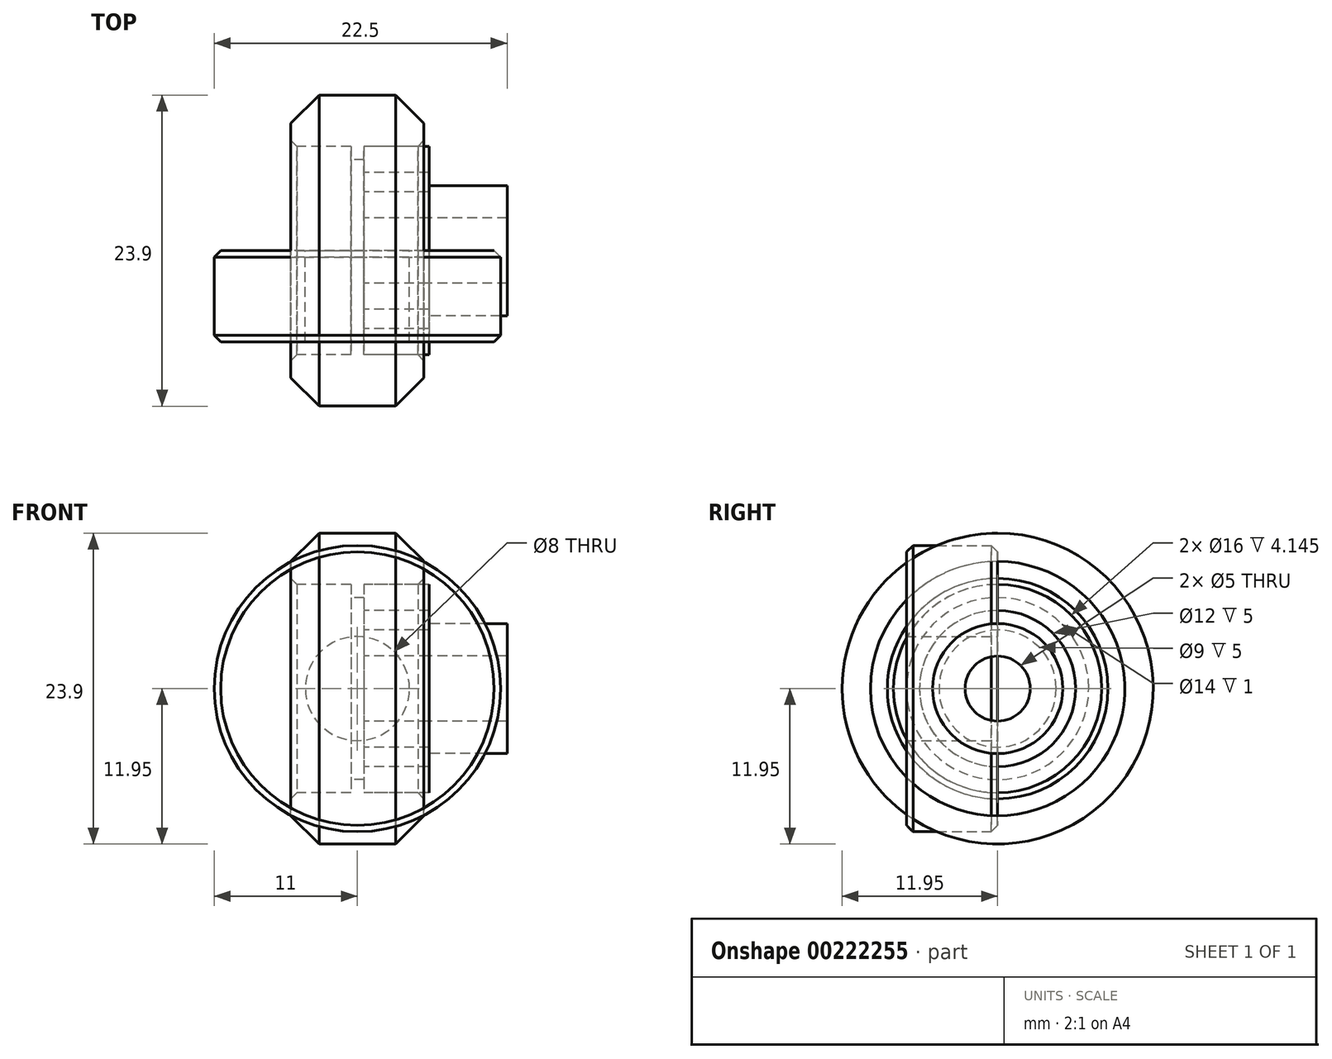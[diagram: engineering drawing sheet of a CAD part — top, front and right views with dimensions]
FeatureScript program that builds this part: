
annotation { "Feature Type Name" : "Feature", "Feature Type Description" : "" }
export const myFeature = defineFeature(function(context is Context, id is Id, definition is map)
    precondition{}
    {
        {
            var Q0;
            Q0=qCreatedBy(makeId("Front.planeOp"),FACE);
            var sketch = newSketch(context, id + "F0", { "sketchPlane" : qUnion([Q0])});
            skLineSegment(sketch, "E0", {"start": v(-1.34, 0) * mm, "end": v(1.5, 0) * mm});
            skLineSegment(sketch, "E1", {"start": v(-2.95, 11.95) * mm, "end": v(2.94, 11.95) * mm});
            skLineSegment(sketch, "E2", {"start": v(2.94, 11.94) * mm, "end": v(5.11, 9.77) * mm});
            skLineSegment(sketch, "E3", {"start": v(5.12, 9.77) * mm, "end": v(5.12, 8.47) * mm});
            skLineSegment(sketch, "E4", {"start": v(5.11, 8.47) * mm, "end": v(4.64, 8) * mm});
            skLineSegment(sketch, "E5", {"start": v(4.65, 8) * mm, "end": v(0.5, 8) * mm});
            skLineSegment(sketch, "E6", {"start": v(0.5, 8) * mm, "end": v(0.5, 7) * mm});
            skLineSegment(sketch, "E7", {"start": v(0.5, 7) * mm, "end": v(-0.5, 7) * mm});
            skLineSegment(sketch, "E8", {"start": v(-0.5, 7) * mm, "end": v(-0.5, 8) * mm});
            skLineSegment(sketch, "E9", {"start": v(-0.5, 8) * mm, "end": v(-4.65, 8) * mm});
            skLineSegment(sketch, "E10", {"start": v(-4.65, 8) * mm, "end": v(-5.11, 8.47) * mm});
            skLineSegment(sketch, "E11", {"start": v(-5.12, 8.47) * mm, "end": v(-5.12, 9.77) * mm});
            skLineSegment(sketch, "E12", {"start": v(-5.12, 9.77) * mm, "end": v(-2.95, 11.95) * mm});
            skPoint(sketch, "E13", {"position": v(0, 0) * mm});
            skPoint(sketch, "E13.positionSnap0", {"position": v(0, 7) * mm});
            skSolve(sketch);
        }
        {
            var Q0;
            Q0=qCreatedBy(makeId("Front.planeOp"),FACE);
            var sketch = newSketch(context, id + "F1", { "sketchPlane" : qUnion([Q0])});
            skLineSegment(sketch, "E14", {"start": v(0.5, 8) * mm, "end": v(5.5, 8) * mm});
            skLineSegment(sketch, "E15", {"start": v(5.5, 8) * mm, "end": v(5.5, 6) * mm});
            skLineSegment(sketch, "E16", {"start": v(5.5, 6) * mm, "end": v(0.5, 6) * mm});
            skLineSegment(sketch, "E17", {"start": v(0.5, 6) * mm, "end": v(0.5, 8) * mm});
            skLineSegment(sketch, "E18", {"start": v(0.5, 2.5) * mm, "end": v(5.5, 2.5) * mm});
            skLineSegment(sketch, "E19", {"start": v(0.5, 4.5) * mm, "end": v(5.5, 4.5) * mm});
            skLineSegment(sketch, "E20", {"start": v(0.5, 6) * mm, "end": v(0.5, 4.5) * mm});
            skLineSegment(sketch, "E21", {"start": v(0.5, 4.5) * mm, "end": v(0.5, 2.5) * mm});
            skLineSegment(sketch, "E22", {"start": v(5.5, 6) * mm, "end": v(5.5, 4.5) * mm});
            skLineSegment(sketch, "E23", {"start": v(5.5, 4.5) * mm, "end": v(5.5, 2.5) * mm});
            skLineSegment(sketch, "E24", {"start": v(0, 0) * mm, "end": v(0, 1.42) * mm});
            skSolve(sketch);
        }
        {
            var Q0;
            Q0=qCreatedBy(makeId("Front.planeOp"),FACE);
            var sketch = newSketch(context, id + "F2", { "sketchPlane" : qUnion([Q0])});
            skLineSegment(sketch, "E25", {"start": v(5.5, 2.5) * mm, "end": v(5.5, 5) * mm});
            skLineSegment(sketch, "E26", {"start": v(5.5, 5) * mm, "end": v(11.5, 5) * mm});
            skLineSegment(sketch, "E27", {"start": v(11.5, 5) * mm, "end": v(11.5, 2.5) * mm});
            skLineSegment(sketch, "E28", {"start": v(11.5, 2.5) * mm, "end": v(5.5, 2.5) * mm});
            skSolve(sketch);
        }
        {
            var Q0;
            Q0=makeQuery(id+"F0.imprint","IMPRINT",FACE,{"disambiguationData":[TD([[makeQuery(id+"F0.imprint","IMPRINT",EDGE,{"derivedFrom":sQuery(id+"F0.wireOp",EDGE,"E1")}),-1.0]])]});
            var Q1;
            Q1=sQuery(id+"F0.wireOp",EDGE,"E0");
            revolve(context, id + "F3", {"entities" : qUnion([Q0]), "axis" : qUnion([Q1]), "revolveType" : RevolveType.FULL});
        }
        {
            var Q0;
            Q0=makeQuery(id+"F1.imprint","IMPRINT",FACE,{"disambiguationData":[TD([[makeQuery(id+"F1.imprint","IMPRINT",EDGE,{"derivedFrom":sQuery(id+"F1.wireOp",EDGE,"46488251-68ce-428c-88e7-6fb8d1af45190.MirrorCS")}),1.0]])]});
            var Q1;
            Q1=makeQuery(id+"F1.imprint","IMPRINT",FACE,{"disambiguationData":[TD([[makeQuery(id+"F1.imprint","IMPRINT",EDGE,{"derivedFrom":sQuery(id+"F1.wireOp",EDGE,"E14")}),-1.0]])]});
            var Q2;
            Q2=sQuery(id+"F0.wireOp",EDGE,"E0");
            revolve(context, id + "F4", {"entities" : qUnion([Q0, Q1]), "axis" : qUnion([Q2]), "revolveType" : RevolveType.FULL});
        }
        {
            var Q0;
            Q0=makeQuery(id+"F1.imprint","IMPRINT",FACE,{"disambiguationData":[TD([[makeQuery(id+"F1.imprint","IMPRINT",EDGE,{"derivedFrom":sQuery(id+"F1.wireOp",EDGE,"46488251-68ce-428c-88e7-6fb8d1af45190.MirrorCS")}),-1.0]])]});
            var Q1;
            Q1=makeQuery(id+"F1.imprint","IMPRINT",FACE,{"disambiguationData":[TD([[makeQuery(id+"F1.imprint","IMPRINT",EDGE,{"derivedFrom":sQuery(id+"F1.wireOp",EDGE,"E16")}),1.0]])]});
            var Q2;
            Q2=sQuery(id+"F0.wireOp",EDGE,"E0");
            revolve(context, id + "F5", {"entities" : qUnion([Q0, Q1]), "axis" : qUnion([Q2]), "revolveType" : RevolveType.FULL});
        }
        {
            var Q0;
            Q0=makeQuery(id+"F1.imprint","IMPRINT",FACE,{"disambiguationData":[TD([[makeQuery(id+"F1.imprint","IMPRINT",EDGE,{"derivedFrom":sQuery(id+"F1.wireOp",EDGE,"3c777b73-887d-43de-96a0-d65bb20abdab0.MirrorCS")}),1.0]])]});
            var Q1;
            Q1=makeQuery(id+"F1.imprint","IMPRINT",FACE,{"disambiguationData":[TD([[makeQuery(id+"F1.imprint","IMPRINT",EDGE,{"derivedFrom":sQuery(id+"F1.wireOp",EDGE,"E18")}),1.0]])]});
            var Q2;
            Q2=sQuery(id+"F0.wireOp",EDGE,"E0");
            revolve(context, id + "F6", {"entities" : qUnion([Q0, Q1]), "axis" : qUnion([Q2]), "revolveType" : RevolveType.FULL});
        }
        {
            var Q0;
            Q0=makeQuery(id+"F2.imprint","IMPRINT",FACE,{"disambiguationData":[TD([[makeQuery(id+"F2.imprint","IMPRINT",EDGE,{"derivedFrom":sQuery(id+"F2.wireOp",EDGE,"E25")}),-1.0]])]});
            var Q1;
            Q1=sQuery(id+"F0.wireOp",EDGE,"E0");
            revolve(context, id + "F7", {"entities" : qUnion([Q0]), "axis" : qUnion([Q1]), "revolveType" : RevolveType.FULL});
        }
        {
            var Q0;
            Q0=qCreatedBy(makeId("Front.planeOp"),FACE);
            var sketch = newSketch(context, id + "F8", { "sketchPlane" : qUnion([Q0])});
            skCircle(sketch, "E29", {"center": v(0, 0) * mm, "radius": 4 * mm});
            skCircle(sketch, "E30", {"center": v(0, 0) * mm, "radius": 11 * mm});
            skSolve(sketch);
        }
        {
            var Q0;
            Q0=makeQuery(id+"F8.imprint","IMPRINT",FACE,{"disambiguationData":[TD([[makeQuery(id+"F8.imprint","IMPRINT",EDGE,{"derivedFrom":sQuery(id+"F8.wireOp",EDGE,"E29")}),-1.0]])]});
            extrude(context, id + "F9", {"entities" : qUnion([Q0]), "depth" : 7 * mm});
        }
        {
            var Q0;
            Q0=makeQuery(id+"F9.opExtrude","CAP_EDGE",EDGE,{"disambiguationData":[OSD([sQuery(id+"F8.wireOp",EDGE,"E30")])],"isStart":false});
            var Q1;
            Q1=makeQuery(id+"F9.opExtrude","CAP_EDGE",EDGE,{"disambiguationData":[OSD([sQuery(id+"F8.wireOp",EDGE,"E30")])],"isStart":true});
            chamfer(context, id + "F10", {"entities" : qUnion([Q0, Q1]), "width" : 0.5 * mm, "tangentPropagation" : true});
        }
    });
